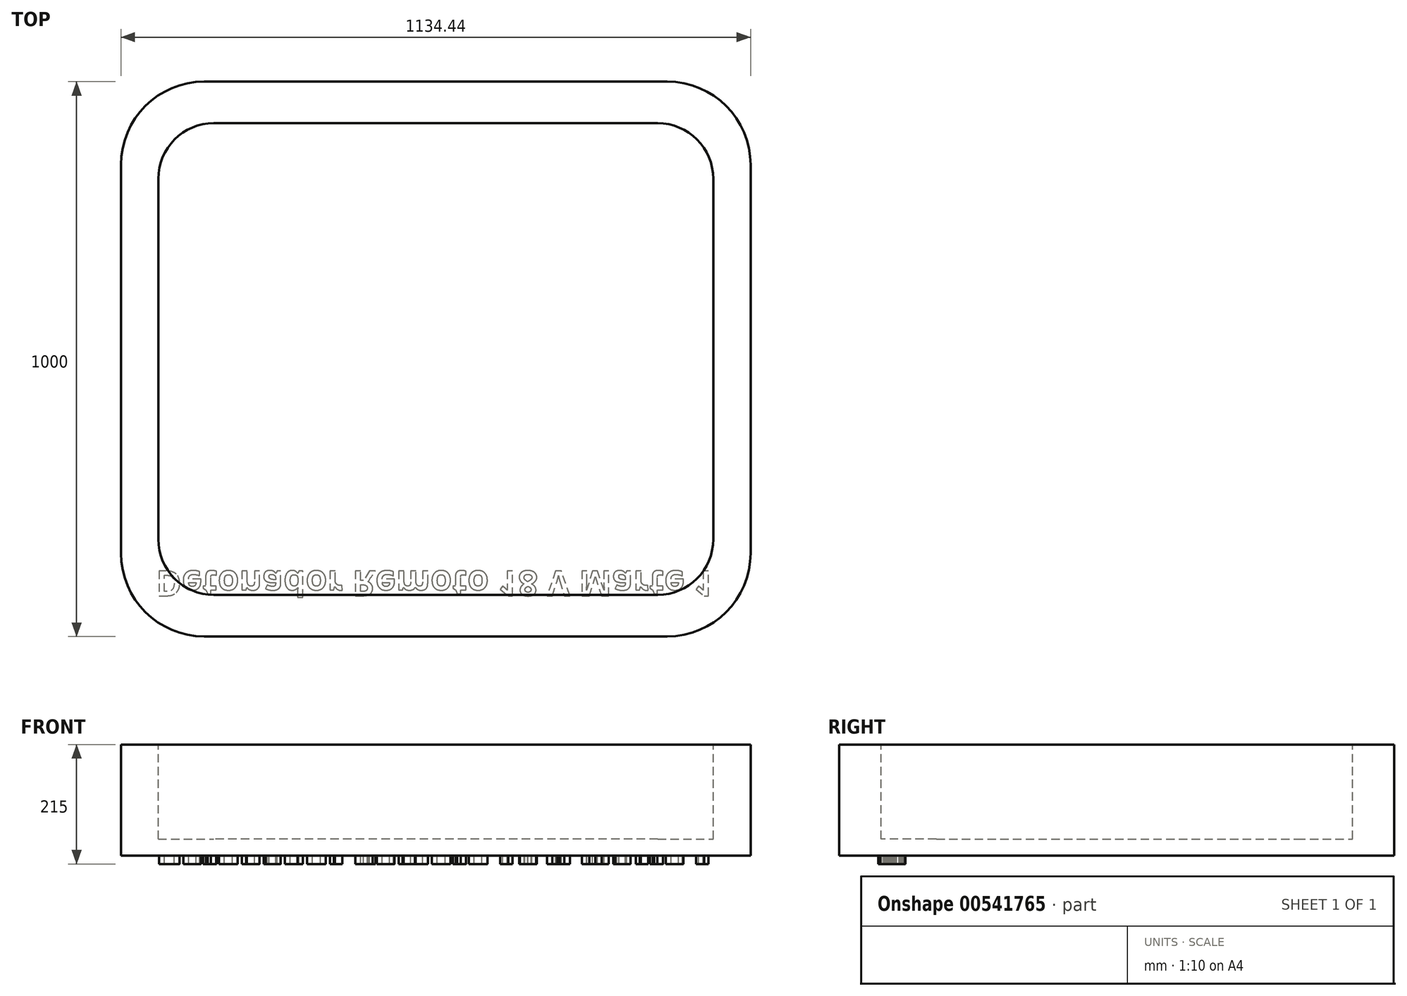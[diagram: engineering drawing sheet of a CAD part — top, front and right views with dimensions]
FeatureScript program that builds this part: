
annotation { "Feature Type Name" : "Feature", "Feature Type Description" : "" }
export const myFeature = defineFeature(function(context is Context, id is Id, definition is map)
    precondition{}
    {
        {
            var Q0;
            Q0=qCreatedBy(makeId("Top.planeOp"),FACE);
            var sketch = newSketch(context, id + "F0", { "sketchPlane" : qUnion([Q0])});
            skLineSegment(sketch, "E0.bottom", {"start": v(567.22, -500) * mm, "end": v(-567.22, -500) * mm});
            skLineSegment(sketch, "E0.top", {"start": v(567.22, 500) * mm, "end": v(-567.22, 500) * mm});
            skLineSegment(sketch, "E0.left", {"start": v(567.22, -500) * mm, "end": v(567.22, 500) * mm});
            skLineSegment(sketch, "E0.right", {"start": v(-567.22, -500) * mm, "end": v(-567.22, 500) * mm});
            skPoint(sketch, "E0.middle", {"position": v(0, 0) * mm});
            skSolve(sketch);
        }
        {
            var Q0;
            Q0=makeQuery(id+"F0.imprint","IMPRINT",FACE,{"disambiguationData":[TD([[makeQuery(id+"F0.imprint","IMPRINT",EDGE,{"derivedFrom":sQuery(id+"F0.wireOp",EDGE,"E0.bottom")}),-1.0]])]});
            extrude(context, id + "F1", {"entities" : qUnion([Q0]), "depth" : 200 * mm, "offsetDistance" : 25 * mm});
        }
        {
            var Q0;
            Q0=makeQuery(id+"F1.opExtrude","SWEPT_EDGE",EDGE,{"disambiguationData":[OSD([sQuery(id+"F0.wireOp",EDGE,"E0.bottom"),sQuery(id+"F0.wireOp",EDGE,"E0.right")])]});
            var Q1;
            Q1=makeQuery(id+"F1.opExtrude","SWEPT_EDGE",EDGE,{"disambiguationData":[OSD([sQuery(id+"F0.wireOp",EDGE,"E0.bottom"),sQuery(id+"F0.wireOp",EDGE,"E0.left")])]});
            var Q2;
            Q2=makeQuery(id+"F1.opExtrude","SWEPT_EDGE",EDGE,{"disambiguationData":[OSD([sQuery(id+"F0.wireOp",EDGE,"E0.top"),sQuery(id+"F0.wireOp",EDGE,"E0.left")])]});
            var Q3;
            Q3=makeQuery(id+"F1.opExtrude","SWEPT_EDGE",EDGE,{"disambiguationData":[OSD([sQuery(id+"F0.wireOp",EDGE,"E0.top"),sQuery(id+"F0.wireOp",EDGE,"E0.right")])]});
            fillet(context, id + "F2", {"entities" : qUnion([Q0, Q1, Q2, Q3]), "radius" : 150 * mm, "tangentPropagation" : true, "allowEdgeOverflow" : false});
        }
        {
            var Q0;
            Q0=makeQuery(id+"F1.opExtrude","CAP_FACE",FACE,{"disambiguationData":[OSD([sQuery(id+"F0.wireOp",EDGE,"E0.bottom"),sQuery(id+"F0.wireOp",EDGE,"E0.top"),sQuery(id+"F0.wireOp",EDGE,"E0.left"),sQuery(id+"F0.wireOp",EDGE,"E0.right")])],"isStart":false});
            var sketch = newSketch(context, id + "F3", { "sketchPlane" : qUnion([Q0])});
            skLineSegment(sketch, "E1.bottom", {"start": v(500, -425) * mm, "end": v(-500, -425) * mm});
            skLineSegment(sketch, "E1.top", {"start": v(500, 425) * mm, "end": v(-500, 425) * mm});
            skLineSegment(sketch, "E1.left", {"start": v(500, -425) * mm, "end": v(500, 425) * mm});
            skLineSegment(sketch, "E1.right", {"start": v(-500, -425) * mm, "end": v(-500, 425) * mm});
            skPoint(sketch, "E1.middle", {"position": v(0, 0) * mm});
            skSolve(sketch);
        }
        {
            var Q0;
            Q0=makeQuery(id+"F3.imprint","IMPRINT",FACE,{"disambiguationData":[TD([[makeQuery(id+"F3.imprint","IMPRINT",EDGE,{"derivedFrom":sQuery(id+"F3.wireOp",EDGE,"E1.bottom")}),-1.0]])]});
            extrude(context, id + "F4", {"entities" : qUnion([Q0]), "operationType" : NewBodyOperationType.REMOVE, "oppositeDirection" : true, "depth" : 170 * mm, "offsetDistance" : 25 * mm});
        }
        {
            var Q0;
            Q0=makeQuery(id+"F4.boolean.opBoolean","COPY",EDGE,{"derivedFrom":makeQuery(id+"F4.opExtrude","SWEPT_EDGE",EDGE,{"disambiguationData":[OSD([sQuery(id+"F3.wireOp",EDGE,"E1.top"),sQuery(id+"F3.wireOp",EDGE,"E1.left")])]})});
            var Q1;
            Q1=makeQuery(id+"F4.boolean.opBoolean","COPY",EDGE,{"derivedFrom":makeQuery(id+"F4.opExtrude","SWEPT_EDGE",EDGE,{"disambiguationData":[OSD([sQuery(id+"F3.wireOp",EDGE,"E1.bottom"),sQuery(id+"F3.wireOp",EDGE,"E1.left")])]})});
            var Q2;
            Q2=makeQuery(id+"F4.boolean.opBoolean","COPY",EDGE,{"derivedFrom":makeQuery(id+"F4.opExtrude","SWEPT_EDGE",EDGE,{"disambiguationData":[OSD([sQuery(id+"F3.wireOp",EDGE,"E1.top"),sQuery(id+"F3.wireOp",EDGE,"E1.right")])]})});
            var Q3;
            Q3=makeQuery(id+"F4.boolean.opBoolean","COPY",EDGE,{"derivedFrom":makeQuery(id+"F4.opExtrude","SWEPT_EDGE",EDGE,{"disambiguationData":[OSD([sQuery(id+"F3.wireOp",EDGE,"E1.bottom"),sQuery(id+"F3.wireOp",EDGE,"E1.right")])]})});
            fillet(context, id + "F5", {"entities" : qUnion([Q0, Q1, Q2, Q3]), "radius" : 100 * mm, "tangentPropagation" : true, "allowEdgeOverflow" : false});
        }
        {
            var Q0;
            Q0=makeQuery(id+"F1.opExtrude","CAP_FACE",FACE,{"disambiguationData":[OSD([sQuery(id+"F0.wireOp",EDGE,"E0.bottom"),sQuery(id+"F0.wireOp",EDGE,"E0.top"),sQuery(id+"F0.wireOp",EDGE,"E0.left"),sQuery(id+"F0.wireOp",EDGE,"E0.right")])],"isStart":true});
            var sketch = newSketch(context, id + "F6", { "sketchPlane" : qUnion([Q0])});
            skText(sketch, "E2", { "text": "Detonador Remoto 18 V Marte 1", "fontName": "OpenSans-Bold.ttf"});
            const initialGuessF6  = {"E2": [-0.50458, 0.38173, 1, 0, 0.04542]};
            skSetInitialGuess(sketch, initialGuessF6);
            skSolve(sketch);
        }
        {
            var Q0;
            Q0 = qSketchRegion(id + "F6", true);
            extrude(context, id + "F7", {"entities" : qUnion([Q0]), "operationType" : NewBodyOperationType.ADD, "depth" : 15 * mm, "offsetDistance" : 25 * mm});
        }
    });
